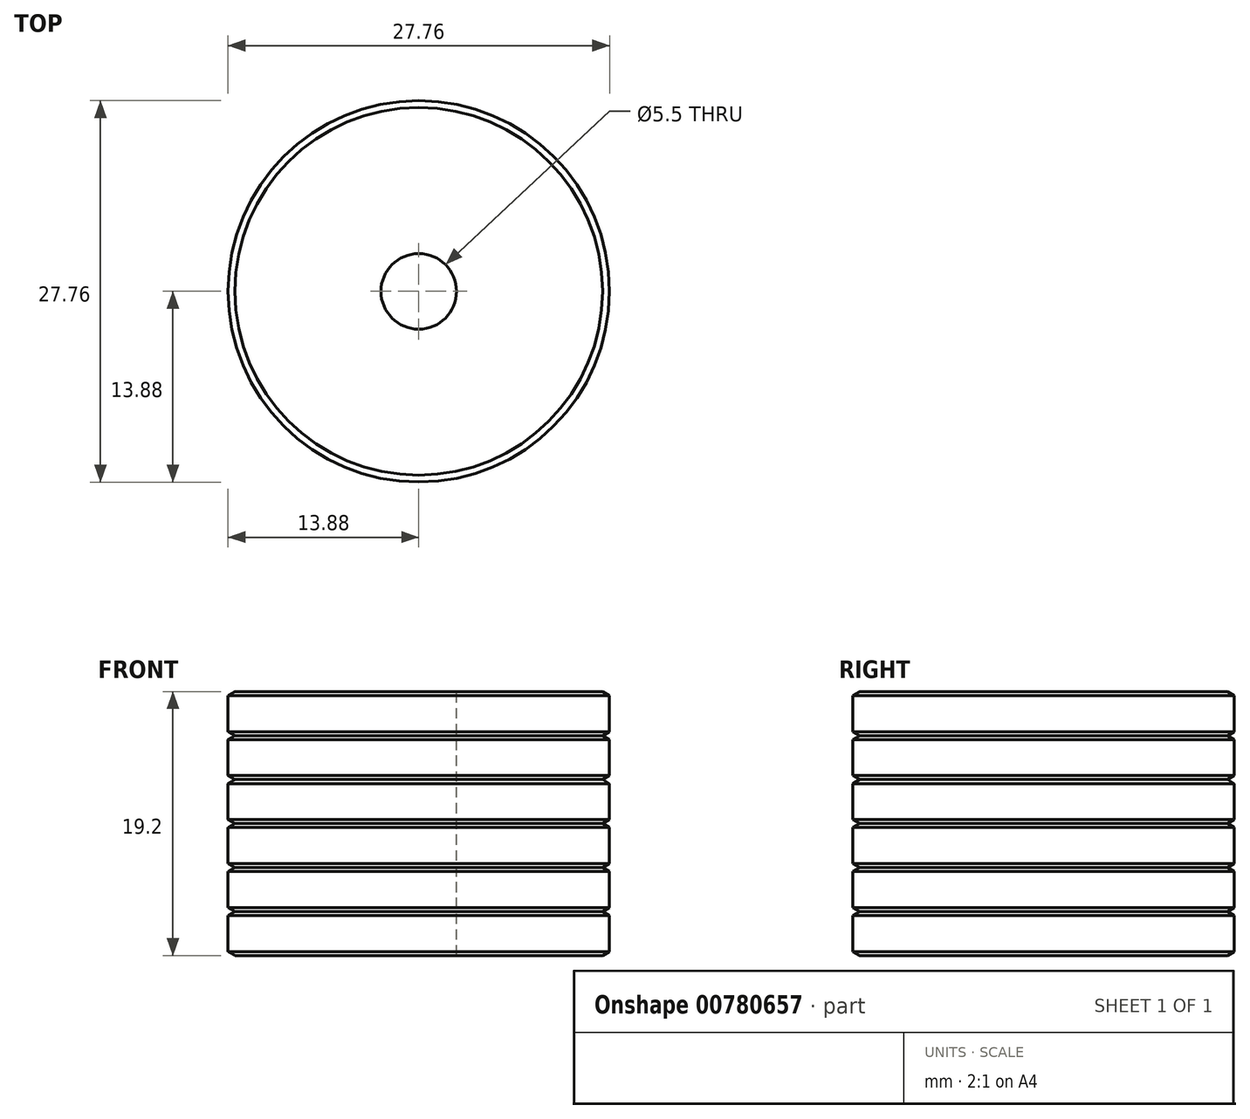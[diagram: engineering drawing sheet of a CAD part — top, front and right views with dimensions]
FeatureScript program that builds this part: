
annotation { "Feature Type Name" : "Feature", "Feature Type Description" : "" }
export const myFeature = defineFeature(function(context is Context, id is Id, definition is map)
    precondition{}
    {
        {
            var Q0;
            Q0=qCreatedBy(makeId("Front.planeOp"),FACE);
            var sketch = newSketch(context, id + "F0", { "sketchPlane" : qUnion([Q0])});
            skLineSegment(sketch, "E0", {"start": v(0, 0) * mm, "end": v(0, 9.6) * mm});
            skLineSegment(sketch, "E1", {"start": v(0, 0) * mm, "end": v(0, -9.6) * mm});
            skLineSegment(sketch, "E2", {"start": v(0, 9.6) * mm, "end": v(13.88, 9.6) * mm});
            skLineSegment(sketch, "E3", {"start": v(13.88, 9.6) * mm, "end": v(13.88, 6.4) * mm});
            skLineSegment(sketch, "E4", {"start": v(13.88, 6.4) * mm, "end": v(13.88, 3.2) * mm});
            skLineSegment(sketch, "E5", {"start": v(13.88, 3.2) * mm, "end": v(13.88, 0) * mm});
            skLineSegment(sketch, "E6", {"start": v(13.88, 0) * mm, "end": v(13.88, -3.2) * mm});
            skLineSegment(sketch, "E7", {"start": v(13.88, -3.2) * mm, "end": v(13.88, -6.4) * mm});
            skLineSegment(sketch, "E8", {"start": v(13.88, -6.4) * mm, "end": v(13.88, -9.6) * mm});
            skLineSegment(sketch, "E9", {"start": v(0, -9.6) * mm, "end": v(13.88, -9.6) * mm});
            skLineSegment(sketch, "E10", {"start": v(13.88, 9.6) * mm, "end": v(13.38, 9.6) * mm});
            skLineSegment(sketch, "E11", {"start": v(13.88, 6.4) * mm, "end": v(13.38, 6.4) * mm});
            skLineSegment(sketch, "E12", {"start": v(13.88, 3.2) * mm, "end": v(13.38, 3.2) * mm});
            skLineSegment(sketch, "E13", {"start": v(13.88, 0) * mm, "end": v(13.38, 0) * mm});
            skLineSegment(sketch, "E14", {"start": v(13.88, -3.2) * mm, "end": v(13.38, -3.2) * mm});
            skLineSegment(sketch, "E15", {"start": v(13.88, -6.4) * mm, "end": v(13.38, -6.4) * mm});
            skLineSegment(sketch, "E16", {"start": v(13.88, -9.6) * mm, "end": v(13.38, -9.6) * mm});
            skLineSegment(sketch, "E17", {"start": v(13.38, 9.6) * mm, "end": v(13.88, 9.31) * mm});
            skLineSegment(sketch, "E18", {"start": v(13.38, 6.4) * mm, "end": v(13.88, 6.69) * mm});
            skLineSegment(sketch, "E19", {"start": v(13.38, 3.2) * mm, "end": v(13.88, 3.49) * mm});
            skLineSegment(sketch, "E20", {"start": v(13.38, 3.2) * mm, "end": v(13.88, 2.91) * mm});
            skLineSegment(sketch, "E21", {"start": v(13.38, 6.4) * mm, "end": v(13.88, 6.11) * mm});
            skLineSegment(sketch, "E22", {"start": v(13.38, 0) * mm, "end": v(13.88, 0.29) * mm});
            skLineSegment(sketch, "E23", {"start": v(13.38, 0) * mm, "end": v(13.88, -0.29) * mm});
            skLineSegment(sketch, "E24", {"start": v(13.38, -3.2) * mm, "end": v(13.88, -2.91) * mm});
            skLineSegment(sketch, "E25", {"start": v(13.38, -3.2) * mm, "end": v(13.88, -3.49) * mm});
            skLineSegment(sketch, "E26", {"start": v(13.38, -6.4) * mm, "end": v(13.88, -6.11) * mm});
            skLineSegment(sketch, "E27", {"start": v(13.38, -6.4) * mm, "end": v(13.88, -6.69) * mm});
            skLineSegment(sketch, "E28", {"start": v(13.38, -9.6) * mm, "end": v(13.88, -9.31) * mm});
            skSolve(sketch);
        }
        {
            var Q0;
            Q0=makeQuery(id+"F0.imprint","IMPRINT",FACE,{"disambiguationData":[TD([[makeQuery(id+"F0.imprint","IMPRINT",EDGE,{"derivedFrom":sQuery(id+"F0.wireOp",EDGE,"E0")}),-1.0]])]});
            var Q1;
            Q1=sQuery(id+"F0.wireOp",EDGE,"E0");
            revolve(context, id + "F1", {"surfaceOperationType" : NewSurfaceOperationType.NEW, "entities" : qUnion([Q0]), "axis" : qUnion([Q1]), "revolveType" : RevolveType.FULL});
        }
        {
            var Q0;
            Q0=makeQuery(id+"F1.opRevolve","SWEPT_FACE",FACE,{"disambiguationData":[OSD([sQuery(id+"F0.wireOp",EDGE,"E2")])]});
            var sketch = newSketch(context, id + "F2", { "sketchPlane" : qUnion([Q0])});
            skCircle(sketch, "E29", {"center": v(0, 0) * mm, "radius": 2.75 * mm});
            skSolve(sketch);
        }
        {
            var Q0;
            Q0 = qSketchRegion(id + "F2", true);
            extrude(context, id + "F3", {"entities" : qUnion([Q0]), "operationType" : NewBodyOperationType.REMOVE, "endBound" : BoundingType.THROUGH_ALL, "oppositeDirection" : true, "depth" : 25 * mm, "offsetDistance" : 25 * mm});
        }
    });
